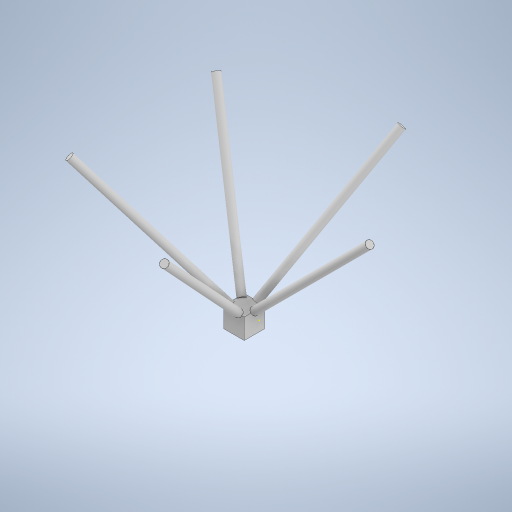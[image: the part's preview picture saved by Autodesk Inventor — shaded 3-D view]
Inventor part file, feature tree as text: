
AUTODESK INVENTOR PART (.ipt)
format: ipt  version: 2024 (Build 280153020, 153B)  size: 275,968 bytes
history: native  units: in
note: dims shown in document units (in); Inventor stores cm internally (conversion verified against a paired STEP export)
features: sketch x3, extrude x2, plane x1, pattern_circular x1
ambient origin geometry x8: Origin, YZ Plane, XZ Plane, XY Plane, X Axis, Y Axis, Z Axis, Center Point
bodies: Body1 (feature_tree)
feature tree (7):
  extrude  "Extrusion2"  Depth=0.9843in
  plane  "Work Plane1"
  sketch  "Sketch4"  dims[d6=0.9843in d7=0.0in d8=45.0deg]
  sketch  "Sketch5"  dims[d9=0.3543in d10=7.874in d11=0.0in d12=1.9685in d13=360.0deg]
  extrude  "Extrusion3"  TaperAngle=45.0deg  [1 undecoded]
  pattern_circular  "Circular Pattern1"  Count=20  [1 undecoded]
  sketch  "Sketch3"  dims[d4=0.9843in d5=0.9843in]
note: 2 required parameter values undecoded (feature->parameter linkage not recoverable at this tier; creation-order binding heuristic only, values carry confidence <= 0.55)
